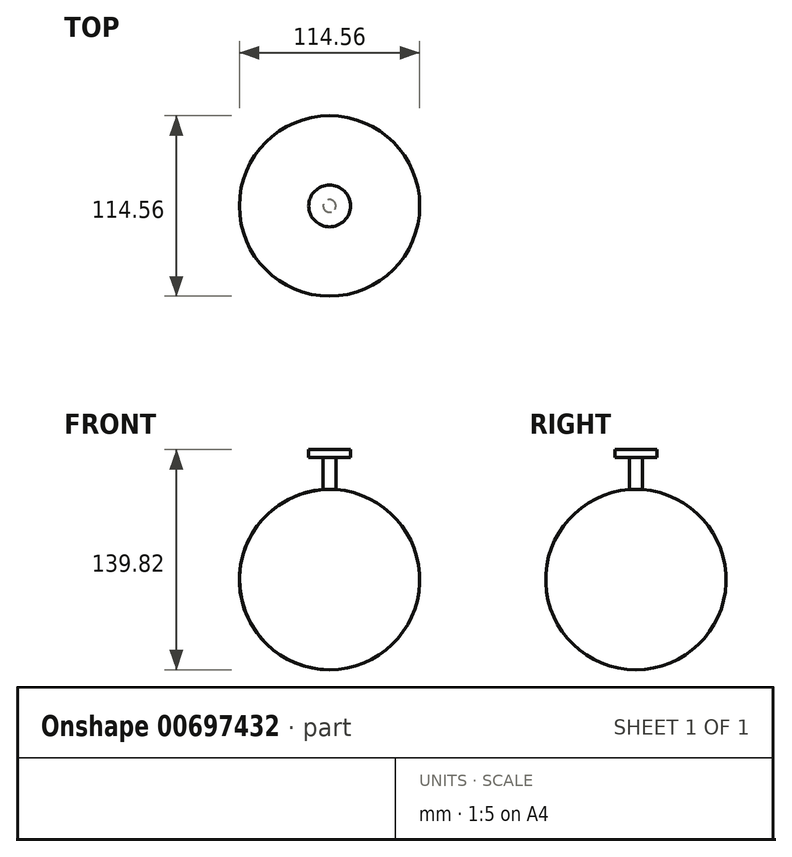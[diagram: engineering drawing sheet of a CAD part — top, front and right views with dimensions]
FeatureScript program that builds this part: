
annotation { "Feature Type Name" : "Feature", "Feature Type Description" : "" }
export const myFeature = defineFeature(function(context is Context, id is Id, definition is map)
    precondition{}
    {
        {
            var Q0;
            Q0=qCreatedBy(makeId("Front.planeOp"),FACE);
            var sketch = newSketch(context, id + "F0", { "sketchPlane" : qUnion([Q0])});
            skLineSegment(sketch, "E0", {"start": v(0, 92.63) * mm, "end": v(0, -98.73) * mm, "construction": true});
            skArc(sketch, "E1", {"start": v(-4.03, 57.14) * mm, "mid": v(-57.24, -2.02) * mm, "end": v(0, -57.28) * mm});
            skLineSegment(sketch, "E2", {"start": v(-4.03, 57.14) * mm, "end": v(-4.03, 77.46) * mm});
            skLineSegment(sketch, "E3", {"start": v(-4.03, 77.46) * mm, "end": v(-13.25, 77.46) * mm});
            skLineSegment(sketch, "E4", {"start": v(-13.25, 77.46) * mm, "end": v(-13.25, 82.54) * mm});
            skLineSegment(sketch, "E5", {"start": v(-13.25, 82.54) * mm, "end": v(0, 82.54) * mm});
            skLineSegment(sketch, "E6", {"start": v(0, 82.54) * mm, "end": v(0, 55.39) * mm});
            skLineSegment(sketch, "E7", {"start": v(0, 55.39) * mm, "end": v(-4.03, 57.14) * mm});
            skLineSegment(sketch, "E8", {"start": v(0, 55.39) * mm, "end": v(0, -57.28) * mm});
            skSolve(sketch);
        }
        {
            var Q0;
            Q0 = qSketchRegion(id + "F0", true);
            var Q1;
            Q1=sQuery(id+"F0.wireOp",EDGE,"E0");
            revolve(context, id + "F1", {"entities" : qUnion([Q0]), "axis" : qUnion([Q1]), "revolveType" : RevolveType.FULL});
        }
    });
